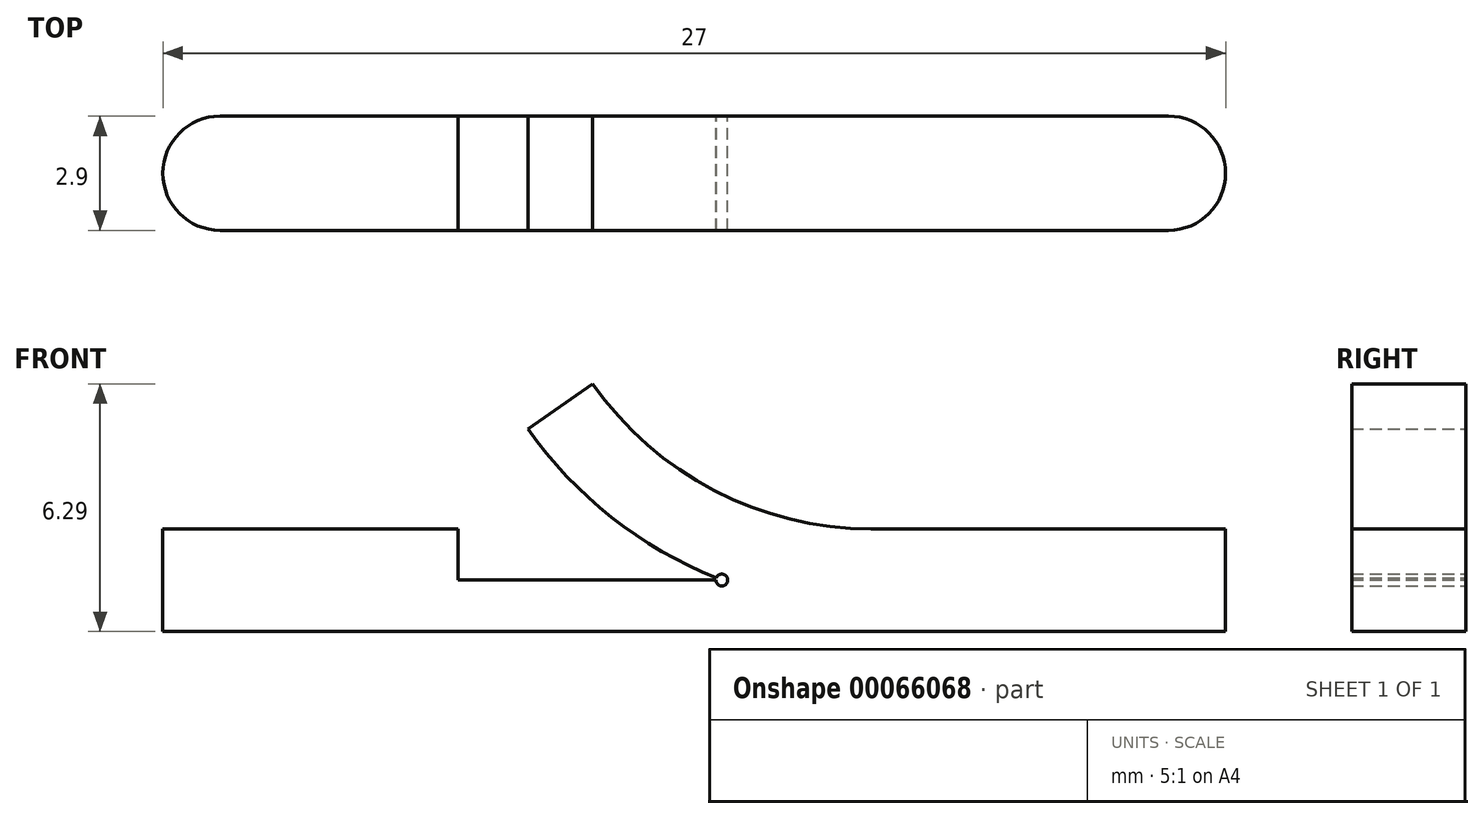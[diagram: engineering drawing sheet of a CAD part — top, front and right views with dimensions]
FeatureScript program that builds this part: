
annotation { "Feature Type Name" : "Feature", "Feature Type Description" : "" }
export const myFeature = defineFeature(function(context is Context, id is Id, definition is map)
    precondition{}
    {
        {
            var Q0;
            Q0=qCreatedBy(makeId("Front.planeOp"),FACE);
            var sketch = newSketch(context, id + "F0", { "sketchPlane" : qUnion([Q0])});
            skCircle(sketch, "E0", {"center": v(0, 0) * mm, "radius": 8.64 * mm, "construction": true});
            skLineSegment(sketch, "E1", {"start": v(0, -8.64) * mm, "end": v(9, -8.64) * mm});
            skLineSegment(sketch, "E2", {"start": v(9, -8.64) * mm, "end": v(9, -11.24) * mm});
            skLineSegment(sketch, "E3", {"start": v(9, -11.24) * mm, "end": v(-18, -11.24) * mm});
            skLineSegment(sketch, "E4", {"start": v(-18, -11.24) * mm, "end": v(-18, -8.64) * mm});
            skLineSegment(sketch, "E5", {"start": v(-18, -8.64) * mm, "end": v(-10.5, -8.64) * mm});
            skLineSegment(sketch, "E6", {"start": v(-10.5, -8.64) * mm, "end": v(-10.5, -9.94) * mm});
            skLineSegment(sketch, "E7", {"start": v(-10.5, -9.94) * mm, "end": v(0, -9.94) * mm});
            skLineSegment(sketch, "E8", {"start": v(0, -9.94) * mm, "end": v(0, -8.64) * mm});
            skArc(sketch, "E9", {"start": v(0, -8.64) * mm, "mid": v(-3.99, -7.66) * mm, "end": v(-7.07, -4.95) * mm});
            skLineSegment(sketch, "E10", {"start": v(-7.07, -4.95) * mm, "end": v(-8.71, -6.1) * mm});
            skArc(sketch, "E11", {"start": v(-8.71, -6.1) * mm, "mid": v(-6.54, -8.39) * mm, "end": v(-3.8, -9.94) * mm});
            skSolve(sketch);
        }
        {
            var Q0;
            Q0=qCreatedBy(makeId("Front.planeOp"),FACE);
            var sketch = newSketch(context, id + "F1", { "sketchPlane" : qUnion([Q0])});
            skPoint(sketch, "E12.0", {"position": v(-3.8, -9.94) * mm});
            skSolve(sketch);
        }
        {
            var Q0;
            Q0 = qSketchRegion(id + "F0", true);
            extrude(context, id + "F2", {"entities" : qUnion([Q0]), "depth" : 2.9 * mm});
        }
        {
            var Q0;
            Q0=makeQuery(id+"F2.opExtrude","CAP_EDGE",EDGE,{"disambiguationData":[OSD([sQuery(id+"F0.wireOp",EDGE,"E2")])],"isStart":false});
            var Q1;
            Q1=makeQuery(id+"F2.opExtrude","CAP_EDGE",EDGE,{"disambiguationData":[OSD([sQuery(id+"F0.wireOp",EDGE,"E2")])],"isStart":true});
            var Q2;
            Q2=makeQuery(id+"F2.opExtrude","CAP_EDGE",EDGE,{"disambiguationData":[OSD([sQuery(id+"F0.wireOp",EDGE,"E4")])],"isStart":false});
            var Q3;
            Q3=makeQuery(id+"F2.opExtrude","CAP_EDGE",EDGE,{"disambiguationData":[OSD([sQuery(id+"F0.wireOp",EDGE,"E4")])],"isStart":true});
            fillet(context, id + "F3", {"entities" : qUnion([Q0, Q1, Q2, Q3]), "radius" : (2.9 / 2) * mm, "allowEdgeOverflow" : false});
        }
        {
            var Q0;
            Q0=sQuery(id+"F1.wireOp",VERTEX,"E12.0");
            var Q1;
            Q1=makeQuery(id+"F2.opExtrude","SWEPT_BODY",BODY,{"disambiguationData":[OSD([sQuery(id+"F0.wireOp",EDGE,"E1"),sQuery(id+"F0.wireOp",EDGE,"E2"),sQuery(id+"F0.wireOp",EDGE,"E3"),sQuery(id+"F0.wireOp",EDGE,"E4"),sQuery(id+"F0.wireOp",EDGE,"E5"),sQuery(id+"F0.wireOp",EDGE,"E6"),sQuery(id+"F0.wireOp",EDGE,"E7"),sQuery(id+"F0.wireOp",EDGE,"E9"),sQuery(id+"F0.wireOp",EDGE,"E10"),sQuery(id+"F0.wireOp",EDGE,"E11")])]});
            hole(context, id + "F4", {"style" : HoleStyle.SIMPLE, "holeDiameter" : 0.3 * mm, "endStyle" : HoleEndStyle.THROUGH, "oppositeDirection" : true, "locations" : qUnion([Q0]), "scope" : qUnion([Q1])});
        }
    });
